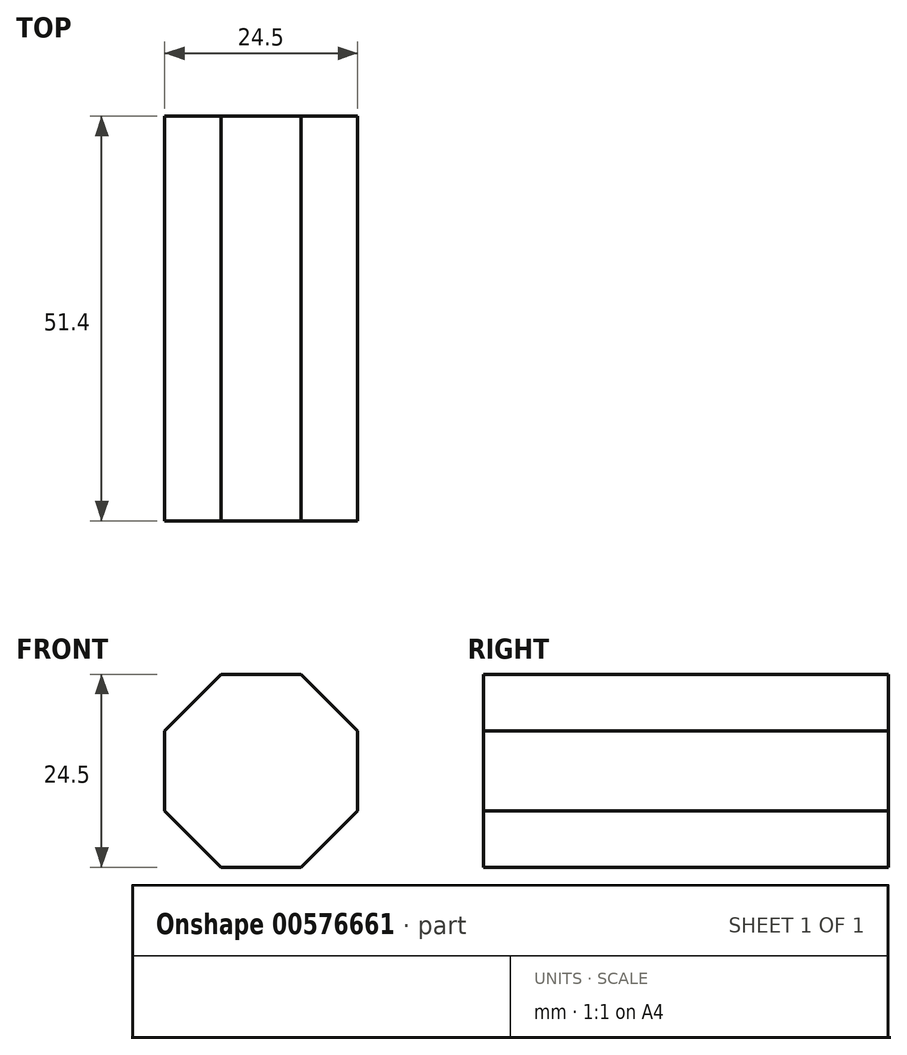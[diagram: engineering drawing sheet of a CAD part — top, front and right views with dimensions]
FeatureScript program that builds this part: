
annotation { "Feature Type Name" : "Feature", "Feature Type Description" : "" }
export const myFeature = defineFeature(function(context is Context, id is Id, definition is map)
    precondition{}
    {
        {
            var Q0;
            Q0=qCreatedBy(makeId("Front.planeOp"),FACE);
            var sketch = newSketch(context, id + "F0", { "sketchPlane" : qUnion([Q0])});
            skCircle(sketch, "E0.cCircle", {"center": v(0, 0) * mm, "radius": 12.25 * mm, "construction": true});
            skLineSegment(sketch, "E0.0", {"start": v(-5.07, 12.25) * mm, "end": v(5.07, 12.25) * mm});
            skLineSegment(sketch, "E0.1", {"start": v(5.07, 12.25) * mm, "end": v(12.25, 5.07) * mm});
            skLineSegment(sketch, "E0.2", {"start": v(12.25, 5.07) * mm, "end": v(12.25, -5.07) * mm});
            skLineSegment(sketch, "E0.3", {"start": v(12.25, -5.07) * mm, "end": v(5.07, -12.25) * mm});
            skLineSegment(sketch, "E0.4", {"start": v(5.07, -12.25) * mm, "end": v(-5.07, -12.25) * mm});
            skLineSegment(sketch, "E0.5", {"start": v(-5.07, -12.25) * mm, "end": v(-12.25, -5.07) * mm});
            skLineSegment(sketch, "E0.6", {"start": v(-12.25, -5.07) * mm, "end": v(-12.25, 5.07) * mm});
            skLineSegment(sketch, "E0.7", {"start": v(-12.25, 5.07) * mm, "end": v(-5.07, 12.25) * mm});
            skPoint(sketch, "E0.0.midPoint", {"position": v(0, 12.25) * mm});
            skSolve(sketch);
        }
        {
            var Q0;
            Q0 = qSketchRegion(id + "F0", true);
            extrude(context, id + "F1", {"entities" : qUnion([Q0]), "depth" : 51.4 * mm, "offsetDistance" : 25.4 * mm});
        }
    });
